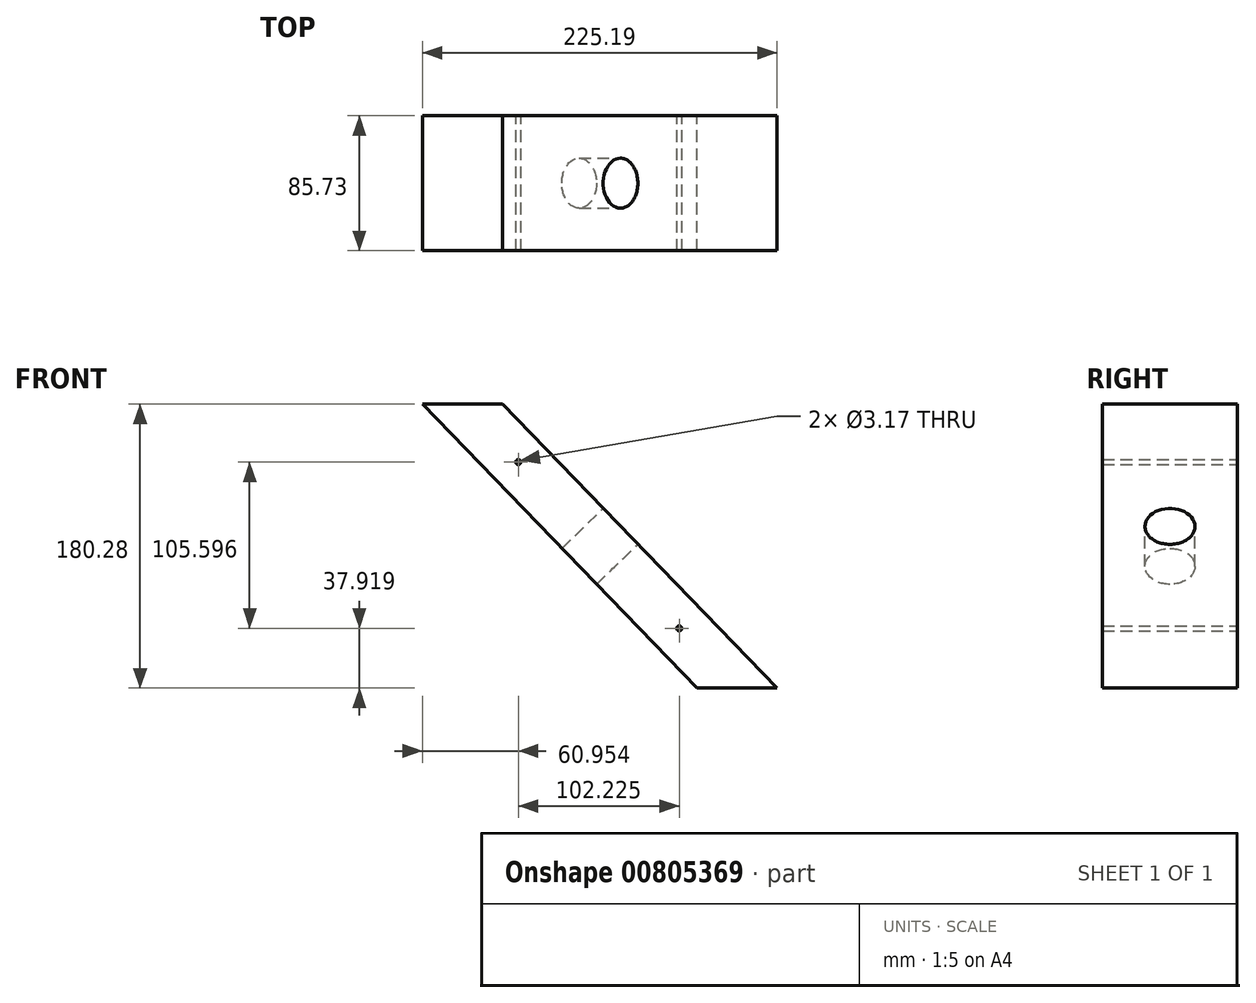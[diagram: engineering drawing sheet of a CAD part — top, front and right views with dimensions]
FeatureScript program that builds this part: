
annotation { "Feature Type Name" : "Feature", "Feature Type Description" : "" }
export const myFeature = defineFeature(function(context is Context, id is Id, definition is map)
    precondition{}
    {
        {
            var Q0;
            Q0=qCreatedBy(makeId("Front.planeOp"),FACE);
            var sketch = newSketch(context, id + "F0", { "sketchPlane" : qUnion([Q0])});
            skLineSegment(sketch, "E0", {"start": v(-118.4, 80.26) * mm, "end": v(-67.6, 80.26) * mm});
            skLineSegment(sketch, "E1", {"start": v(-67.6, 80.26) * mm, "end": v(106.78, -100.02) * mm});
            skLineSegment(sketch, "E2", {"start": v(106.78, -100.02) * mm, "end": v(55.98, -100.02) * mm});
            skLineSegment(sketch, "E3", {"start": v(55.98, -100.02) * mm, "end": v(-118.4, 80.26) * mm});
            skSolve(sketch);
        }
        {
            var Q0;
            Q0=makeQuery(id+"F0.imprint","IMPRINT",FACE,{"disambiguationData":[TD([[makeQuery(id+"F0.imprint","IMPRINT",EDGE,{"derivedFrom":sQuery(id+"F0.wireOp",EDGE,"E0")}),-1.0]])]});
            extrude(context, id + "F1", {"entities" : qUnion([Q0]), "depth" : 85.72 * mm, "offsetDistance" : 25.4 * mm});
        }
        {
            var Q0;
            Q0=makeQuery(id+"F1.opExtrude","SWEPT_FACE",FACE,{"disambiguationData":[OSD([sQuery(id+"F0.wireOp",EDGE,"E1")])]});
            var sketch = newSketch(context, id + "F2", { "sketchPlane" : qUnion([Q0])});
            skCircle(sketch, "E4", {"center": v(-42.86, -3.26) * mm, "radius": 15.88 * mm});
            skLineSegment(sketch, "E5", {"start": v(-85.73, -3.26) * mm, "end": v(0, -3.26) * mm});
            skSolve(sketch);
        }
        {
            var Q0;
            {var subQ0=sQuery(id+"F2.wireOp",EDGE,"E5");var subQ1=sQuery(id+"F2.wireOp",EDGE,"E4");var subQ2=makeQuery(id+"F2.imprint","INTERSECT",VERTEX,{"disambiguationData":[OD(0.0)],"derivedFrom":[subQ1,subQ0]});Q0=makeQuery(id+"F2.imprint","IMPRINT",FACE,{"disambiguationData":[TD([[makeQuery(id+"F2.imprint","IMPRINT",EDGE,{"disambiguationData":[TD([[subQ2,-1.0]])],"derivedFrom":subQ1}),1.0]])]});}
            var Q1;
            {var subQ0=sQuery(id+"F2.wireOp",EDGE,"E5");var subQ1=sQuery(id+"F2.wireOp",EDGE,"E4");var subQ2=makeQuery(id+"F2.imprint","INTERSECT",VERTEX,{"disambiguationData":[OD(0.0)],"derivedFrom":[subQ1,subQ0]});Q1=makeQuery(id+"F2.imprint","IMPRINT",FACE,{"disambiguationData":[TD([[makeQuery(id+"F2.imprint","IMPRINT",EDGE,{"disambiguationData":[TD([[subQ2,1.0]])],"derivedFrom":subQ1}),1.0]])]});}
            extrude(context, id + "F3", {"entities" : qUnion([Q0, Q1]), "operationType" : NewBodyOperationType.REMOVE, "oppositeDirection" : true, "depth" : 50.8 * mm, "offsetDistance" : 25.4 * mm});
        }
        {
            var Q0;
            Q0=makeQuery(id+"F1.opExtrude","CAP_FACE",FACE,{"disambiguationData":[OSD([sQuery(id+"F0.wireOp",EDGE,"E0"),sQuery(id+"F0.wireOp",EDGE,"E1"),sQuery(id+"F0.wireOp",EDGE,"E2"),sQuery(id+"F0.wireOp",EDGE,"E3")])],"isStart":true});
            var sketch = newSketch(context, id + "F4", { "sketchPlane" : qUnion([Q0])});
            skPoint(sketch, "E6.endSnap0", {"position": v(75.4, 61.48) * mm});
            skCircle(sketch, "E7", {"center": v(-44.77, -62.1) * mm, "radius": 1.59 * mm});
            skCircle(sketch, "E8", {"center": v(57.46, 43.5) * mm, "radius": 1.59 * mm});
            skSolve(sketch);
        }
        {
            var Q0;
            Q0=makeQuery(id+"F4.imprint","IMPRINT",FACE,{"disambiguationData":[TD([[makeQuery(id+"F4.imprint","IMPRINT",EDGE,{"derivedFrom":sQuery(id+"F4.wireOp",EDGE,"E7")}),1.0]])]});
            var Q1;
            Q1=makeQuery(id+"F4.imprint","IMPRINT",FACE,{"disambiguationData":[TD([[makeQuery(id+"F4.imprint","IMPRINT",EDGE,{"derivedFrom":sQuery(id+"F4.wireOp",EDGE,"E8")}),1.0]])]});
            extrude(context, id + "F5", {"entities" : qUnion([Q0, Q1]), "operationType" : NewBodyOperationType.REMOVE, "oppositeDirection" : true, "depth" : 127 * mm, "offsetDistance" : 25.4 * mm});
        }
    });
